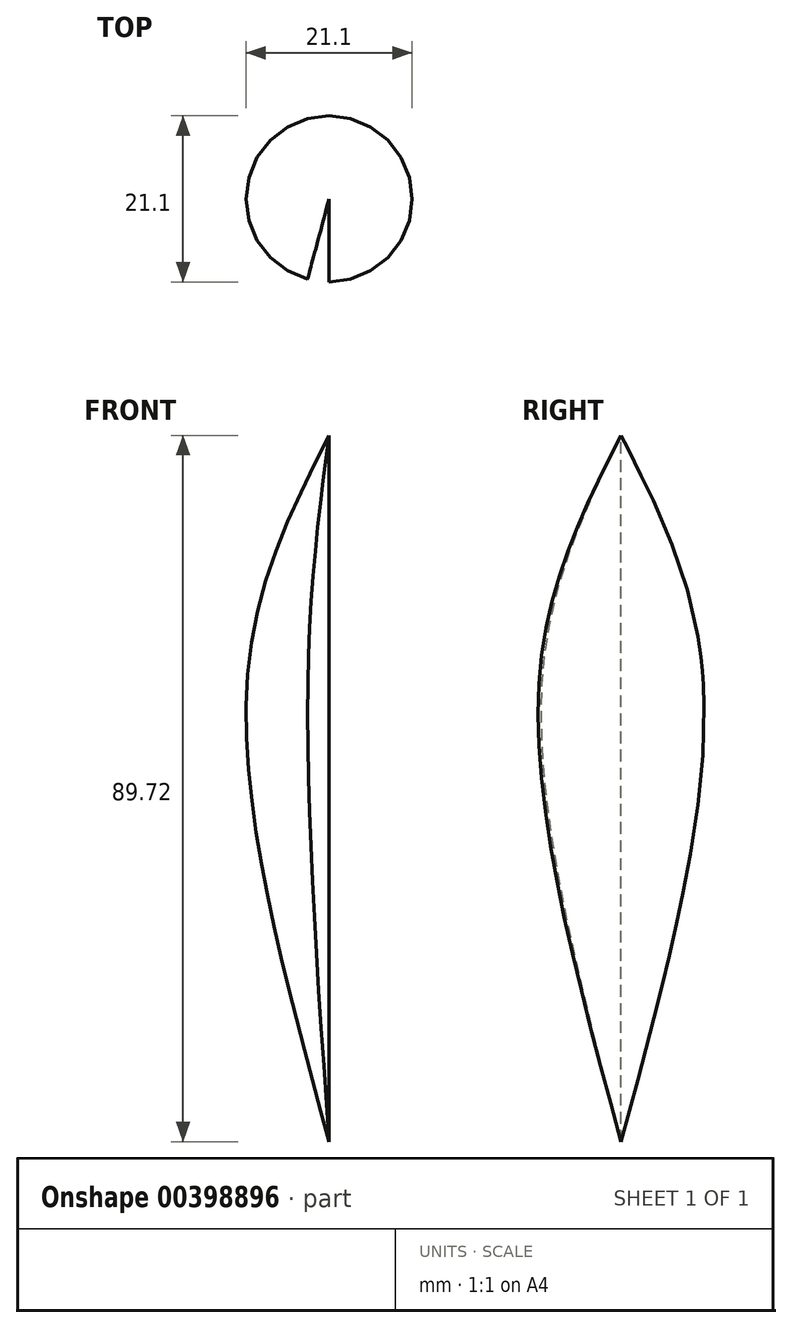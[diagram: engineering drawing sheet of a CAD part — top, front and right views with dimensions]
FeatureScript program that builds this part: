
annotation { "Feature Type Name" : "Feature", "Feature Type Description" : "" }
export const myFeature = defineFeature(function(context is Context, id is Id, definition is map)
    precondition{}
    {
        {
            var Q0;
            Q0=qCreatedBy(makeId("Right.planeOp"),FACE);
            var sketch = newSketch(context, id + "F0", { "sketchPlane" : qUnion([Q0])});
            skLineSegment(sketch, "E0", {"start": v(42.13, -33.75) * mm, "end": v(42.13, 55.97) * mm});
            skFitSpline(sketch, "E1", {"points": [v(42.13, 55.97) * mm, v(31.75, 25.37) * mm, v(42.13, -33.75) * mm], "startDerivative": vector(-33.52, -65.92) * mm, "endDerivative": vector(30.26, -111.2) * mm});
            skSolve(sketch);
        }
        {
            var Q0;
            Q0=makeQuery(id+"F0.imprint","IMPRINT",FACE,{"disambiguationData":[TD([[makeQuery(id+"F0.imprint","IMPRINT",EDGE,{"derivedFrom":sQuery(id+"F0.wireOp",EDGE,"E0")}),1.0]])]});
            var Q1;
            Q1=sQuery(id+"F0.wireOp",EDGE,"E0");
            revolve(context, id + "F1", {"entities" : qUnion([Q0]), "axis" : qUnion([Q1]), "revolveType" : RevolveType.ONE_DIRECTION, "angle" : 345 * degree});
        }
    });
